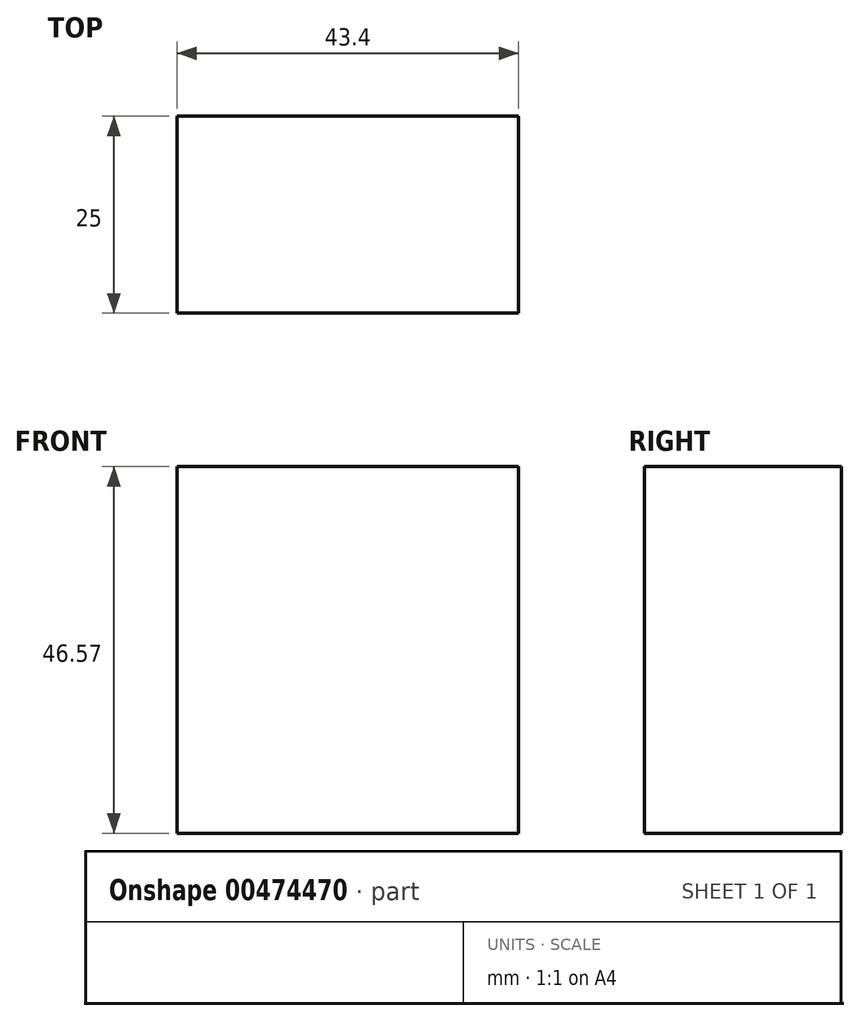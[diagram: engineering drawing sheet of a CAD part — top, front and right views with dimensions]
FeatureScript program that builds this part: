
annotation { "Feature Type Name" : "Feature", "Feature Type Description" : "" }
export const myFeature = defineFeature(function(context is Context, id is Id, definition is map)
    precondition{}
    {
        {
            var Q0;
            Q0=qCreatedBy(makeId("Front.planeOp"),FACE);
            var sketch = newSketch(context, id + "F0", { "sketchPlane" : qUnion([Q0])});
            skLineSegment(sketch, "E0.bottom", {"start": v(-98.47, 5.96) * mm, "end": v(-55.07, 5.96) * mm});
            skLineSegment(sketch, "E0.top", {"start": v(-98.47, 52.53) * mm, "end": v(-55.07, 52.53) * mm});
            skLineSegment(sketch, "E0.left", {"start": v(-98.47, 5.96) * mm, "end": v(-98.47, 52.53) * mm});
            skLineSegment(sketch, "E0.right", {"start": v(-55.07, 5.96) * mm, "end": v(-55.07, 52.53) * mm});
            skPoint(sketch, "E0.middle", {"position": v(-76.77, 29.24) * mm});
            skSolve(sketch);
        }
        {
            var Q0;
            Q0=makeQuery(id+"F0.imprint","IMPRINT",FACE,{"disambiguationData":[TD([[makeQuery(id+"F0.imprint","IMPRINT",EDGE,{"derivedFrom":sQuery(id+"F0.wireOp",EDGE,"E0.bottom")}),1.0]])]});
            extrude(context, id + "F1", {"entities" : qUnion([Q0]), "depth" : 25 * mm});
        }
    });
